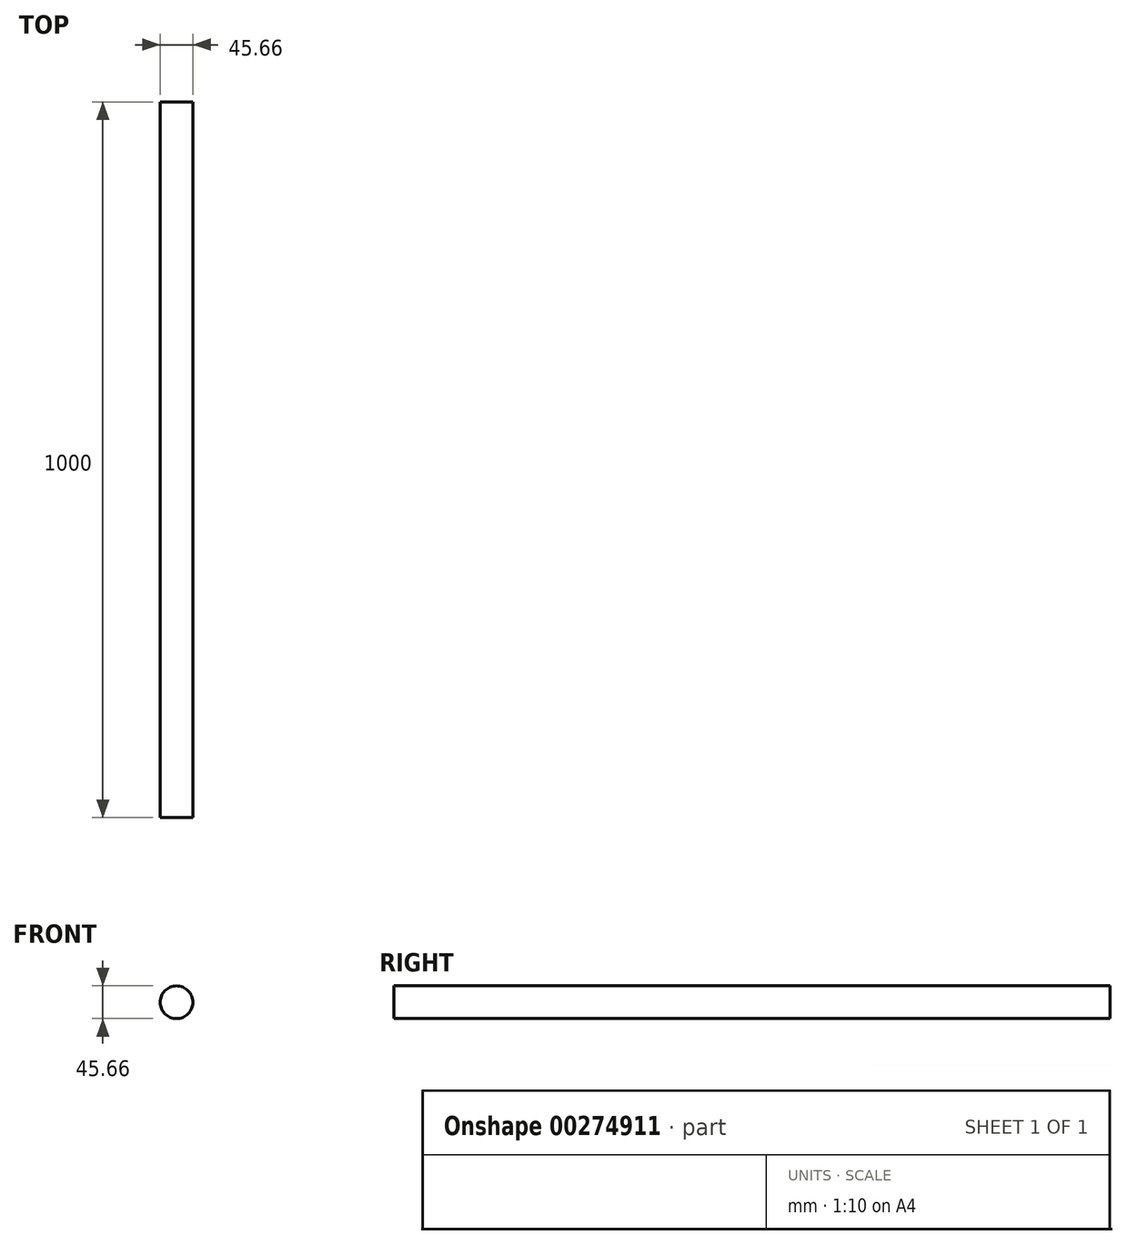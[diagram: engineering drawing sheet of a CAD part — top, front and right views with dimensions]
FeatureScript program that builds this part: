
annotation { "Feature Type Name" : "Feature", "Feature Type Description" : "" }
export const myFeature = defineFeature(function(context is Context, id is Id, definition is map)
    precondition{}
    {
        {
            var Q0;
            Q0=qCreatedBy(makeId("Front.planeOp"),FACE);
            var sketch = newSketch(context, id + "F0", { "sketchPlane" : qUnion([Q0])});
            skCircle(sketch, "E0", {"center": v(0, 0) * mm, "radius": 22.83 * mm});
            skSolve(sketch);
        }
        {
            var Q0;
            Q0 = qSketchRegion(id + "F0", true);
            extrude(context, id + "F1", {"entities" : qUnion([Q0]), "depth" : 1000 * mm});
        }
    });
